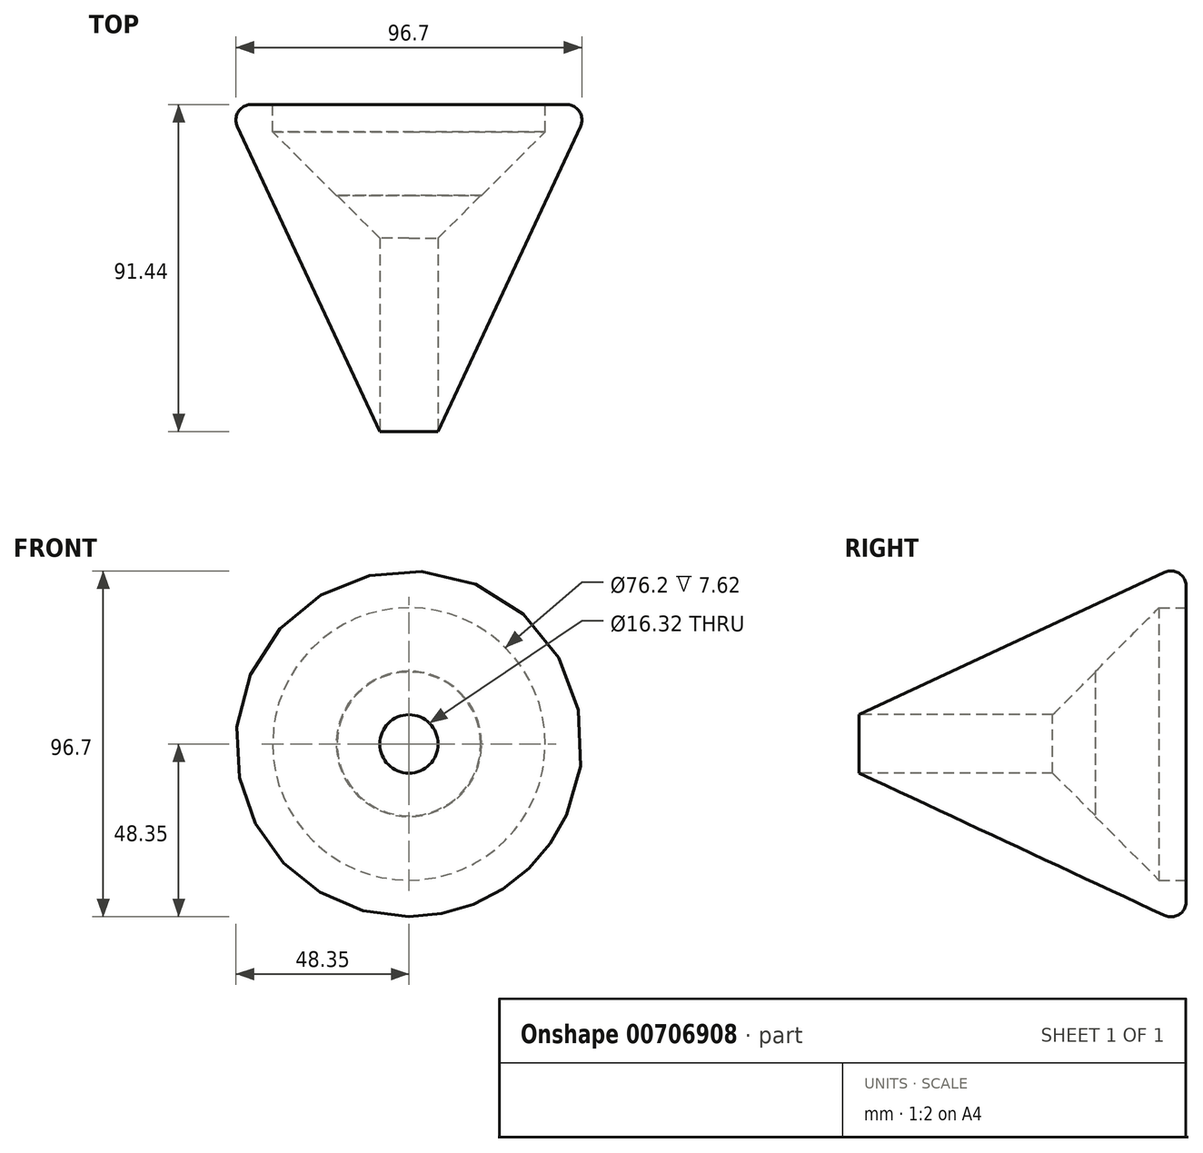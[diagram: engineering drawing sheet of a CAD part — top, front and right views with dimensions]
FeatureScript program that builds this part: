
annotation { "Feature Type Name" : "Feature", "Feature Type Description" : "" }
export const myFeature = defineFeature(function(context is Context, id is Id, definition is map)
    precondition{}
    {
        {
            var Q0;
            Q0=qCreatedBy(makeId("Front.planeOp"),FACE);
            var sketch = newSketch(context, id + "F0", { "sketchPlane" : qUnion([Q0])});
            skCircle(sketch, "E0", {"center": v(0, 0) * mm, "radius": 50.8 * mm});
            skSolve(sketch);
        }
        {
            var Q0;
            Q0=makeQuery(id+"F0.imprint","IMPRINT",FACE,{"disambiguationData":[TD([[makeQuery(id+"F0.imprint","IMPRINT",EDGE,{"derivedFrom":sQuery(id+"F0.wireOp",EDGE,"E0")}),1.0]])]});
            extrude(context, id + "F1", {"entities" : qUnion([Q0]), "depth" : 91.44 * mm, "offsetDistance" : 25.4 * mm, "hasDraft" : true, "draftAngle" : 25 * degree, "draftPullDirection" : true});
        }
        {
            var Q0;
            Q0=makeQuery(id+"F1.opExtrude","CAP_FACE",FACE,{"disambiguationData":[OSD([sQuery(id+"F0.wireOp",EDGE,"E0")])],"isStart":true});
            var sketch = newSketch(context, id + "F2", { "sketchPlane" : qUnion([Q0])});
            skCircle(sketch, "E1", {"center": v(0, 0) * mm, "radius": 38.1 * mm});
            skSolve(sketch);
        }
        {
            var Q0;
            Q0=makeQuery(id+"F2.imprint","IMPRINT",FACE,{"disambiguationData":[TD([[makeQuery(id+"F2.imprint","IMPRINT",EDGE,{"derivedFrom":sQuery(id+"F2.wireOp",EDGE,"E1")}),1.0]])]});
            extrude(context, id + "F3", {"entities" : qUnion([Q0]), "operationType" : NewBodyOperationType.REMOVE, "oppositeDirection" : true, "depth" : 25.4 * mm, "offsetDistance" : 25.4 * mm});
        }
        {
            var Q0;
            Q0=makeQuery(id+"F1.opExtrude","CAP_EDGE",EDGE,{"disambiguationData":[OSD([sQuery(id+"F0.wireOp",EDGE,"E0")])],"isStart":true});
            var Q1;
            Q1=makeQuery(id+"F3.boolean.opBoolean","COPY",EDGE,{"derivedFrom":makeQuery(id+"F3.opExtrude","CAP_EDGE",EDGE,{"disambiguationData":[OSD([sQuery(id+"F2.wireOp",EDGE,"E1")])],"isStart":true})});
            fillet(context, id + "F4", {"entities" : qUnion([Q0, Q1]), "radius" : 4.3 * mm, "tangentPropagation" : true, "allowEdgeOverflow" : false});
        }
        {
            var Q0;
            {var subQ0=sQuery(id+"F2.wireOp",EDGE,"E1");Q0=makeQuery(id+"F4.opFillet","BLEND_EDGE",EDGE,{"blendedFrom":[makeQuery(id+"F3.boolean.opBoolean","COPY",EDGE,{"derivedFrom":makeQuery(id+"F3.opExtrude","CAP_EDGE",EDGE,{"disambiguationData":[OSD([subQ0])],"isStart":true})}),makeQuery(id+"F3.boolean.opBoolean","COPY",FACE,{"derivedFrom":makeQuery(id+"F3.opExtrude","SWEPT_FACE",FACE,{"disambiguationData":[OSD([subQ0])]})})],"blendedInto":[makeQuery(id+"F3.boolean.opBoolean","COPY",FACE,{"derivedFrom":makeQuery(id+"F3.opExtrude","SWEPT_FACE",FACE,{"disambiguationData":[OSD([subQ0])]})})]});}
            var Q1;
            Q1=makeQuery(id+"F3.boolean.opBoolean","COPY",EDGE,{"derivedFrom":makeQuery(id+"F3.opExtrude","CAP_EDGE",EDGE,{"disambiguationData":[OSD([sQuery(id+"F2.wireOp",EDGE,"E1")])],"isStart":false})});
            chamfer(context, id + "F5", {"entities" : qUnion([Q0, Q1]), "width" : 17.78 * mm, "tangentPropagation" : true});
        }
        {
            var Q0;
            Q0=makeQuery(id+"F1.opExtrude","CAP_FACE",FACE,{"disambiguationData":[OSD([sQuery(id+"F0.wireOp",EDGE,"E0")])],"isStart":false});
            extrude(context, id + "F6", {"entities" : qUnion([Q0]), "operationType" : NewBodyOperationType.REMOVE, "oppositeDirection" : true, "depth" : 106.17 * mm, "offsetDistance" : 25.4 * mm});
        }
        {
            var Q0;
            Q0=makeQuery(id+"F6.boolean.opBoolean","INTERSECT",EDGE,{"derivedFrom":[makeQuery(id+"F3.boolean.opBoolean","COPY",FACE,{"derivedFrom":makeQuery(id+"F3.opExtrude","CAP_FACE",FACE,{"disambiguationData":[OSD([sQuery(id+"F2.wireOp",EDGE,"E1")])],"isStart":false})}),makeQuery(id+"F6.opExtrude","SWEPT_FACE",FACE,{"disambiguationData":[OSD([sQuery(id+"F0.wireOp",EDGE,"E0")])]})]});
            chamfer(context, id + "F7", {"entities" : qUnion([Q0]), "width" : 11.94 * mm, "tangentPropagation" : true});
        }
    });
